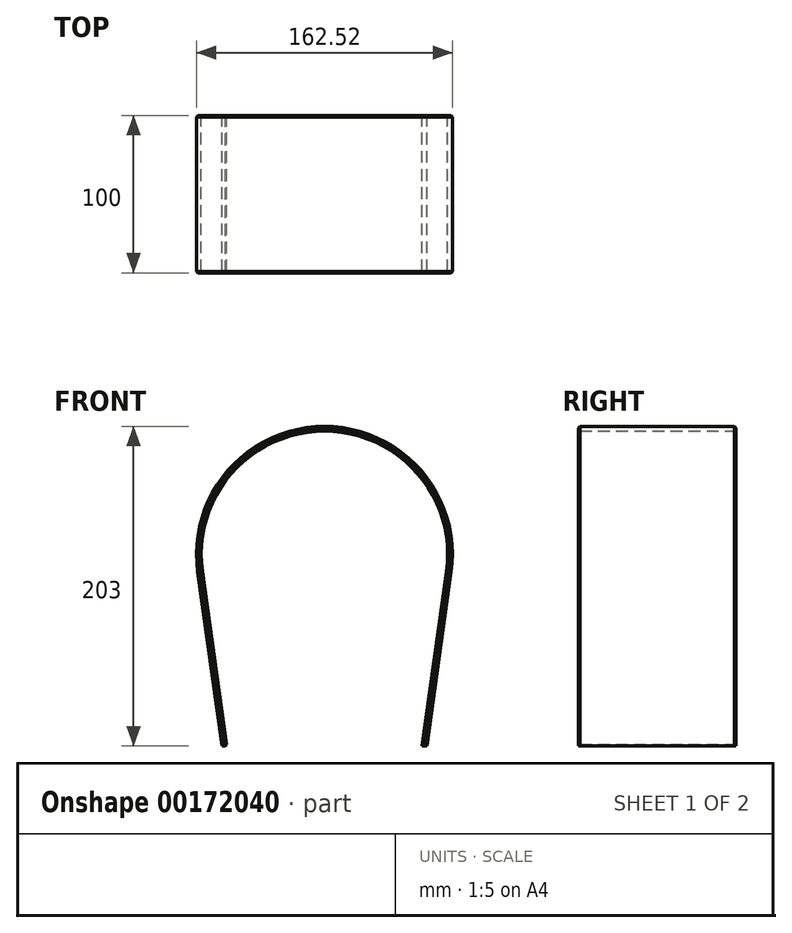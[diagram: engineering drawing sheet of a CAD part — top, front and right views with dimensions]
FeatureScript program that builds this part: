
annotation { "Feature Type Name" : "Feature", "Feature Type Description" : "" }
export const myFeature = defineFeature(function(context is Context, id is Id, definition is map)
    precondition{}
    {
        {
            var Q0;
            Q0=qCreatedBy(makeId("Front.planeOp"),FACE);
            var sketch = newSketch(context, id + "F0", { "sketchPlane" : qUnion([Q0])});
            skLineSegment(sketch, "E0", {"start": v(-77.5, 50.47) * mm, "end": v(-77.5, -46.64) * mm, "construction": true});
            skLineSegment(sketch, "E1", {"start": v(77.5, 44.5) * mm, "end": v(77.5, -57.34) * mm, "construction": true});
            skLineSegment(sketch, "E2", {"start": v(-77.5, 0) * mm, "end": v(77.5, 0) * mm, "construction": true});
            skLineSegment(sketch, "E3", {"start": v(-77.5, 0) * mm, "end": v(-61.92, -110.85) * mm});
            skLineSegment(sketch, "E4", {"start": v(77.5, 0) * mm, "end": v(61.92, -110.85) * mm});
            skArc(sketch, "E5", {"start": v(77.5, 0) * mm, "mid": v(0, 89.15) * mm, "end": v(-77.5, 0) * mm});
            skLineSegment(sketch, "E6", {"start": v(-61.92, -110.85) * mm, "end": v(61.92, -110.85) * mm, "construction": true});
            skLineSegment(sketch, "E7.0", {"start": v(-80.47, -0.42) * mm, "end": v(-64.95, -110.85) * mm});
            skArc(sketch, "E7.1", {"start": v(80.47, -0.42) * mm, "mid": v(0, 92.15) * mm, "end": v(-80.47, -0.42) * mm});
            skLineSegment(sketch, "E7.2", {"start": v(80.47, -0.42) * mm, "end": v(64.95, -110.85) * mm});
            skLineSegment(sketch, "E8", {"start": v(-64.95, -110.85) * mm, "end": v(-61.92, -110.85) * mm});
            skLineSegment(sketch, "E9", {"start": v(61.92, -110.85) * mm, "end": v(64.95, -110.85) * mm});
            skSolve(sketch);
        }
        {
            var Q0;
            Q0 = qSketchRegion(id + "F0", true);
            extrude(context, id + "F1", {"entities" : qUnion([Q0]), "depth" : 100 * mm});
        }
        {
            var Q0;
            Q0=makeQuery(id+"F1.opExtrude","SWEPT_FACE",FACE,{"disambiguationData":[OSD([sQuery(id+"F0.wireOp",EDGE,"E7.1")])]});
            var Q1;
            Q1=makeQuery(id+"F1.opExtrude","SWEPT_FACE",FACE,{"disambiguationData":[OSD([sQuery(id+"F0.wireOp",EDGE,"E5")])]});
            var Q2;
            Q2=makeQuery(id+"F1.opExtrude","SWEPT_FACE",FACE,{"disambiguationData":[OSD([sQuery(id+"F0.wireOp",EDGE,"E3")])]});
            chamfer(context, id + "F2", {"entities" : qUnion([Q0, Q1, Q2]), "width" : 1 * mm, "tangentPropagation" : true});
        }
    });
